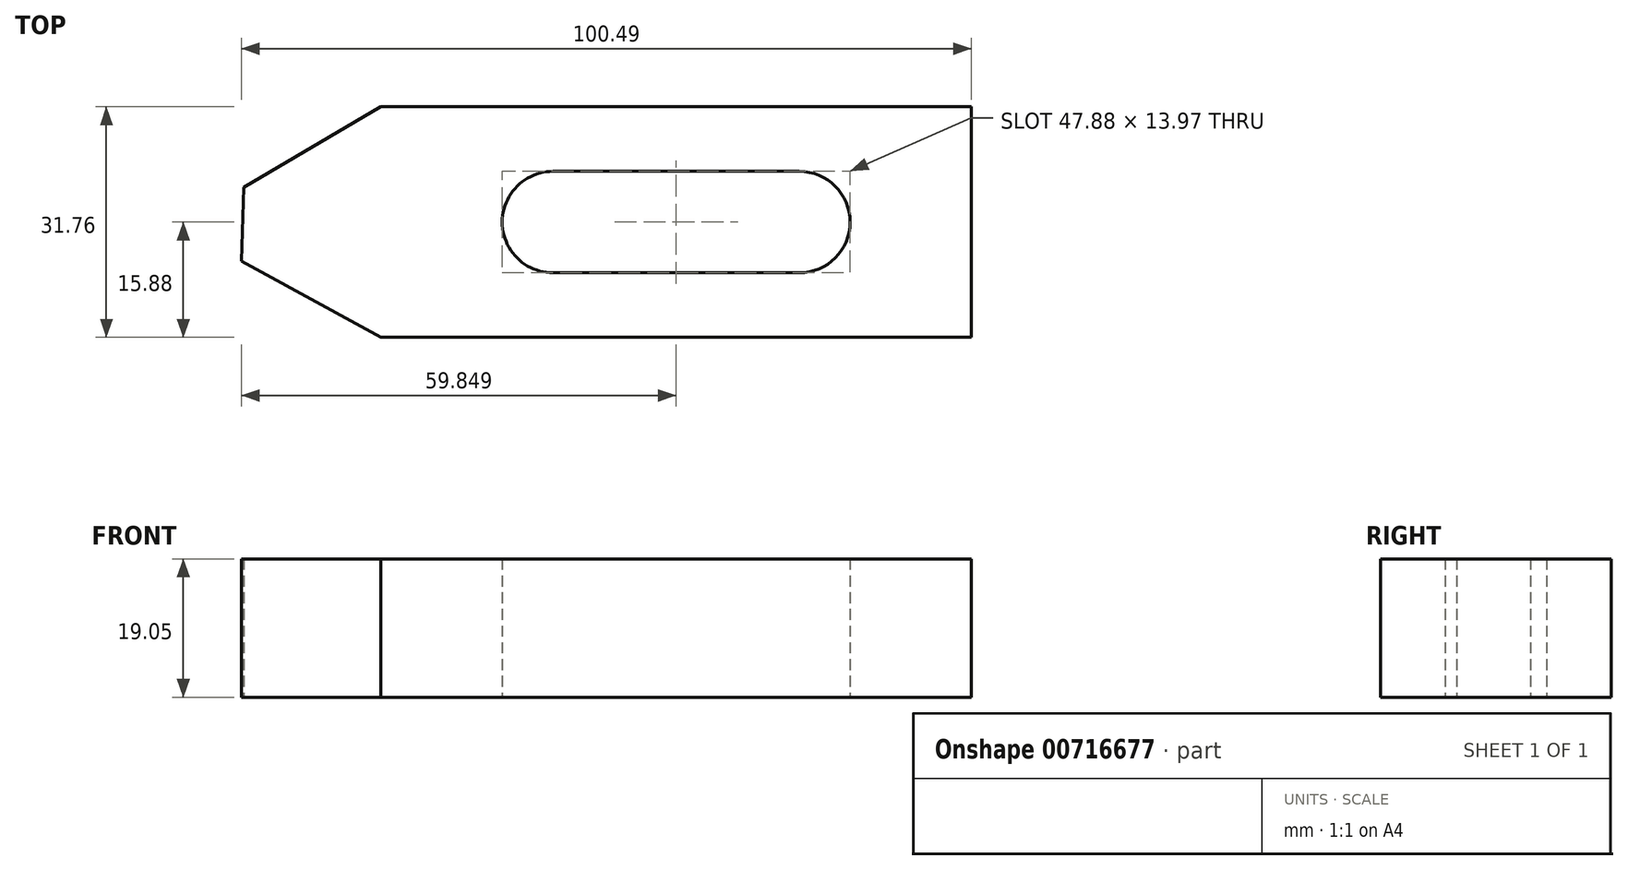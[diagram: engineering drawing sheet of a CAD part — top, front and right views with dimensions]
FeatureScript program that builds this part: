
annotation { "Feature Type Name" : "Feature", "Feature Type Description" : "" }
export const myFeature = defineFeature(function(context is Context, id is Id, definition is map)
    precondition{}
    {
        {
            var Q0;
            Q0=qCreatedBy(makeId("Top.planeOp"),FACE);
            var sketch = newSketch(context, id + "F0", { "sketchPlane" : qUnion([Q0])});
            skLineSegment(sketch, "E0.bottom", {"start": v(40.64, 15.88) * mm, "end": v(-40.64, 15.88) * mm});
            skLineSegment(sketch, "E0.top", {"start": v(40.64, -15.88) * mm, "end": v(-40.64, -15.88) * mm});
            skLineSegment(sketch, "E0.left", {"start": v(40.64, 15.87) * mm, "end": v(40.64, -15.88) * mm});
            skPoint(sketch, "E0.middle", {"position": v(0, 0) * mm});
            skLineSegment(sketch, "E1.right", {"start": v(-59.51, 4.78) * mm, "end": v(-59.85, -5.38) * mm});
            skLineSegment(sketch, "E2", {"start": v(-59.51, 4.78) * mm, "end": v(-40.64, 15.87) * mm});
            skLineSegment(sketch, "E3", {"start": v(-59.85, -5.38) * mm, "end": v(-40.64, -15.88) * mm});
            skLineSegment(sketch, "E4", {"start": v(-40.64, 15.88) * mm, "end": v(-40.64, -15.88) * mm});
            skSolve(sketch);
        }
        {
            var Q0;
            Q0=makeQuery(id+"F0.imprint","IMPRINT",FACE,{"disambiguationData":[TD([[makeQuery(id+"F0.imprint","IMPRINT",EDGE,{"derivedFrom":sQuery(id+"F0.wireOp",EDGE,"E0.bottom")}),1.0]])]});
            extrude(context, id + "F1", {"entities" : qUnion([Q0]), "depth" : 19.05 * mm, "offsetDistance" : 25.4 * mm});
        }
        {
            var Q0;
            Q0=qCreatedBy(makeId("Top.planeOp"),FACE);
            var sketch = newSketch(context, id + "F2", { "sketchPlane" : qUnion([Q0])});
            skLineSegment(sketch, "E5.bottom", {"start": v(-16.96, -6.99) * mm, "end": v(16.95, -6.99) * mm});
            skLineSegment(sketch, "E5.top", {"start": v(-16.95, 6.99) * mm, "end": v(16.96, 6.99) * mm});
            skPoint(sketch, "E5.middle", {"position": v(0, 0) * mm});
            skArc(sketch, "E6", {"start": v(16.95, -6.99) * mm, "mid": v(23.94, 0) * mm, "end": v(16.96, 6.99) * mm});
            skArc(sketch, "E7", {"start": v(-16.96, -6.99) * mm, "mid": v(-23.94, 0) * mm, "end": v(-16.95, 6.99) * mm});
            skSolve(sketch);
        }
        {
            var Q0;
            Q0=makeQuery(id+"F2.imprint","IMPRINT",FACE,{"disambiguationData":[TD([[makeQuery(id+"F2.imprint","IMPRINT",EDGE,{"derivedFrom":sQuery(id+"F2.wireOp",EDGE,"E5.bottom")}),1.0]])]});
            var Q1;
            Q1=sQuery(id+"F2.wireOp",EDGE,"E7");
            var Q2;
            Q2=sQuery(id+"F2.wireOp",EDGE,"E5.top");
            var Q3;
            Q3=sQuery(id+"F2.wireOp",EDGE,"E5.bottom");
            var Q4;
            Q4=sQuery(id+"F2.wireOp",EDGE,"E6");
            extrude(context, id + "F3", {"entities" : qUnion([Q0]), "operationType" : NewBodyOperationType.REMOVE, "surfaceEntities" : qUnion([Q1, Q2, Q3, Q4]), "depth" : 19.3 * mm, "offsetDistance" : 25.4 * mm, "hasSecondDirection" : true, "secondDirectionOppositeDirection" : true, "secondDirectionDepth" : 19.05 * mm});
        }
        {
            var Q0;
            Q0=makeQuery(id+"F0.imprint","IMPRINT",FACE,{"disambiguationData":[TD([[makeQuery(id+"F0.imprint","IMPRINT",EDGE,{"derivedFrom":sQuery(id+"F0.wireOp",EDGE,"E1.right")}),1.0]])]});
            extrude(context, id + "F4", {"entities" : qUnion([Q0]), "operationType" : NewBodyOperationType.ADD, "depth" : 19.05 * mm, "offsetDistance" : 25.4 * mm});
        }
    });
